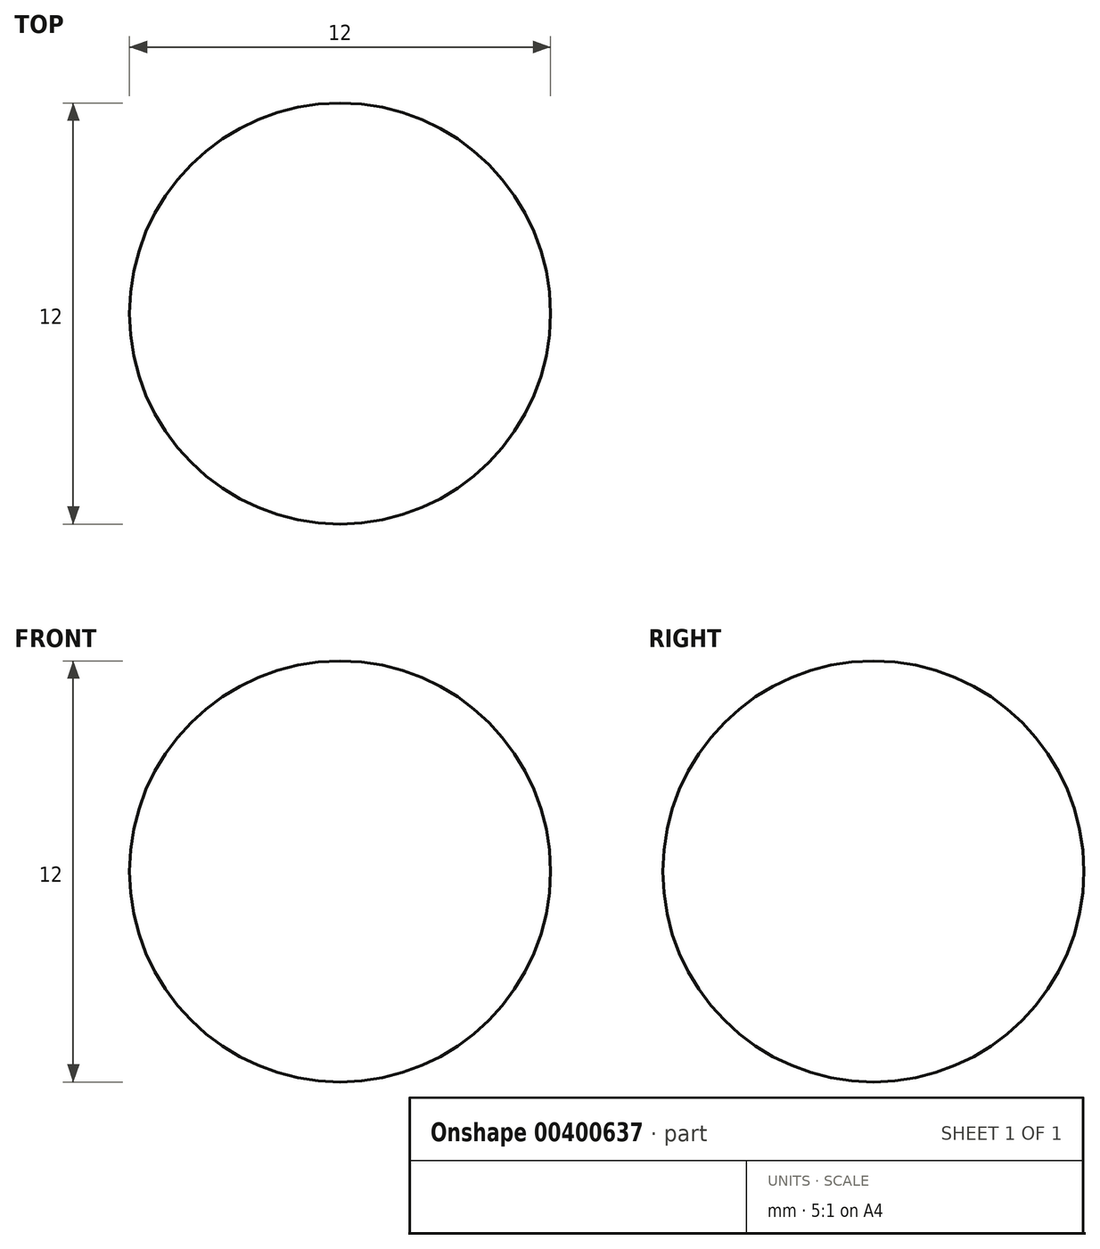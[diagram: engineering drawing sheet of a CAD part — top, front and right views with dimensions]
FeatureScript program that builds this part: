
annotation { "Feature Type Name" : "Feature", "Feature Type Description" : "" }
export const myFeature = defineFeature(function(context is Context, id is Id, definition is map)
    precondition{}
    {
        {
            var Q0;
            Q0=qCreatedBy(makeId("Front.planeOp"),FACE);
            var sketch = newSketch(context, id + "F0", { "sketchPlane" : qUnion([Q0])});
            skArc(sketch, "E0", {"start": v(0, -6) * mm, "mid": v(6, 0) * mm, "end": v(0, 6) * mm});
            skLineSegment(sketch, "E1", {"start": v(0, 6) * mm, "end": v(0, -6) * mm});
            skSolve(sketch);
        }
        {
            var Q0;
            Q0 = qSketchRegion(id + "F0", true);
            var Q1;
            Q1=sQuery(id+"F0.wireOp",EDGE,"E1");
            revolve(context, id + "F1", {"entities" : qUnion([Q0]), "axis" : qUnion([Q1]), "revolveType" : RevolveType.FULL});
        }
    });
